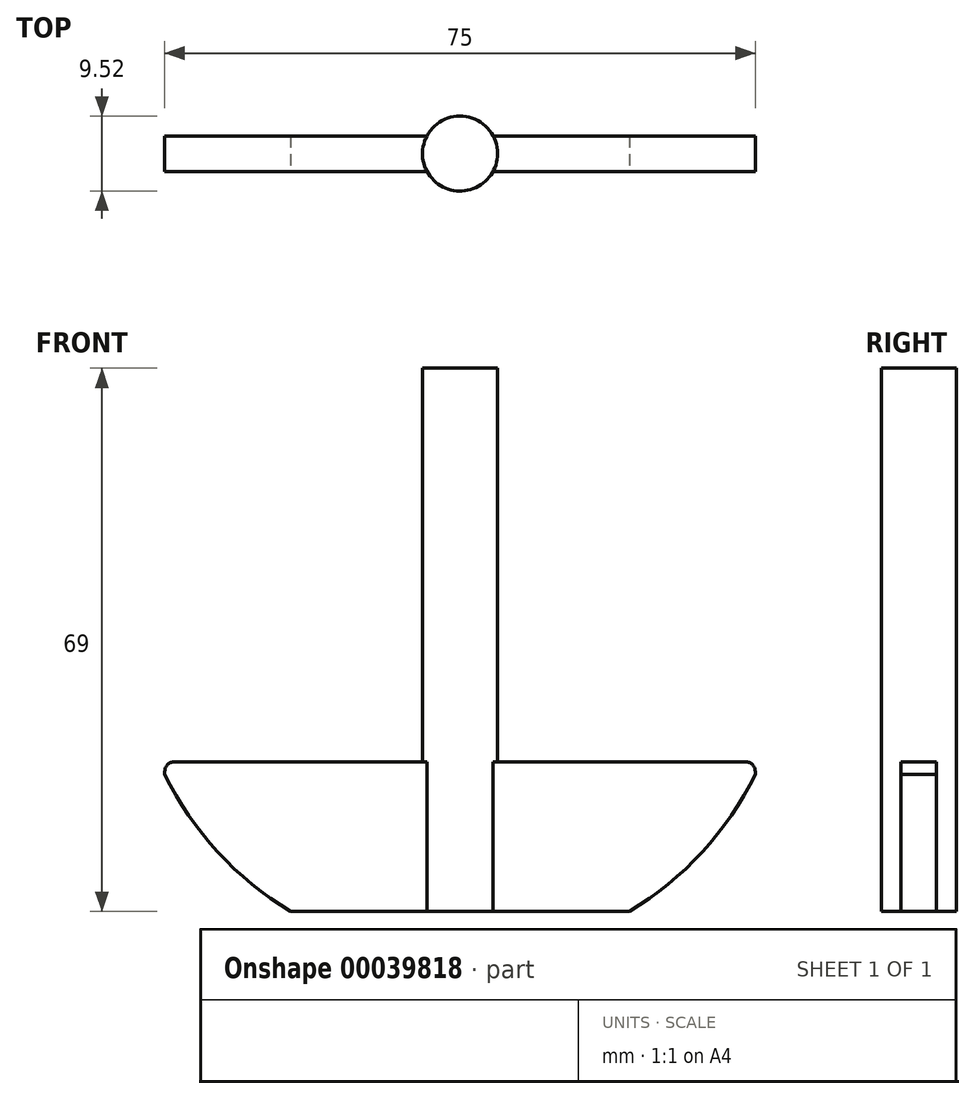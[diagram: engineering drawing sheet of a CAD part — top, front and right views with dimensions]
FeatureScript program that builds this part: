
annotation { "Feature Type Name" : "Feature", "Feature Type Description" : "" }
export const myFeature = defineFeature(function(context is Context, id is Id, definition is map)
    precondition{}
    {
        {
            var Q0;
            Q0=qCreatedBy(makeId("Top.planeOp"),FACE);
            var sketch = newSketch(context, id + "F0", { "sketchPlane" : qUnion([Q0])});
            skLineSegment(sketch, "E0.bottom", {"start": v(-7.96, 2) * mm, "end": v(25.34, 2) * mm});
            skLineSegment(sketch, "E0.top", {"start": v(-7.96, -2.5) * mm, "end": v(25.34, -2.5) * mm});
            skLineSegment(sketch, "E0.left", {"start": v(-7.96, 2) * mm, "end": v(-7.96, -2.5) * mm});
            skLineSegment(sketch, "E0.right", {"start": v(67.04, 2) * mm, "end": v(67.04, -2.5) * mm});
            skLineSegment(sketch, "E1", {"start": v(29.54, 2) * mm, "end": v(29.54, -16.68) * mm, "construction": true});
            skLineSegment(sketch, "E2", {"start": v(-7.96, -0.24) * mm, "end": v(37.53, -0.24) * mm, "construction": true});
            skArc(sketch, "E3", {"start": v(25.34, -2.5) * mm, "mid": v(29.54, -5) * mm, "end": v(33.73, -2.5) * mm});
            skArc(sketch, "E4.trimOffspring", {"start": v(33.73, 2) * mm, "mid": v(29.54, 4.52) * mm, "end": v(25.34, 2) * mm});
            skLineSegment(sketch, "E5.trimOffspring", {"start": v(33.73, 2) * mm, "end": v(67.04, 2) * mm});
            skLineSegment(sketch, "E6.trimOffspring", {"start": v(33.73, -2.5) * mm, "end": v(67.04, -2.5) * mm});
            skSolve(sketch);
        }
        {
            var Q0;
            Q0 = qSketchRegion(id + "F0", true);
            extrude(context, id + "F1", {"entities" : qUnion([Q0]), "depth" : 19 * mm});
        }
        {
            var Q0;
            Q0=makeQuery(id+"F1.opExtrude","CAP_FACE",FACE,{"disambiguationData":[OSD([sQuery(id+"F0.wireOp",EDGE,"E0.bottom"),sQuery(id+"F0.wireOp",EDGE,"E0.top"),sQuery(id+"F0.wireOp",EDGE,"E0.left"),sQuery(id+"F0.wireOp",EDGE,"E0.right"),sQuery(id+"F0.wireOp",EDGE,"E3"),sQuery(id+"F0.wireOp",EDGE,"E4.trimOffspring"),sQuery(id+"F0.wireOp",EDGE,"E5.trimOffspring"),sQuery(id+"F0.wireOp",EDGE,"E6.trimOffspring")])],"isStart":false});
            var sketch = newSketch(context, id + "F2", { "sketchPlane" : qUnion([Q0])});
            skCircle(sketch, "E7", {"center": v(29.54, -0.24) * mm, "radius": 4.76 * mm});
            skSolve(sketch);
        }
        {
            var Q0;
            Q0 = qSketchRegion(id + "F2", true);
            extrude(context, id + "F3", {"entities" : qUnion([Q0]), "operationType" : NewBodyOperationType.ADD, "depth" : 50 * mm});
        }
        {
            var Q0;
            Q0=makeQuery(id+"F1.opExtrude","SWEPT_FACE",FACE,{"disambiguationData":[OSD([sQuery(id+"F0.wireOp",EDGE,"E0.top")])]});
            var sketch = newSketch(context, id + "F4", { "sketchPlane" : qUnion([Q0])});
            skArc(sketch, "E8", {"start": v(-9.13, 19.99) * mm, "mid": v(-2.18, 8.6) * mm, "end": v(8, 0) * mm});
            skLineSegment(sketch, "E9", {"start": v(8, 0) * mm, "end": v(51.07, 0) * mm});
            skArc(sketch, "E10.trimOffspring", {"start": v(51.07, 0) * mm, "mid": v(61.3, 8.67) * mm, "end": v(68.27, 20.14) * mm});
            skLineSegment(sketch, "E11", {"start": v(8, 0) * mm, "end": v(-9.13, 0) * mm});
            skLineSegment(sketch, "E12", {"start": v(-9.13, 0) * mm, "end": v(-9.13, 19.99) * mm});
            skLineSegment(sketch, "E13", {"start": v(51.07, 0) * mm, "end": v(68.75, 0) * mm});
            skLineSegment(sketch, "E14", {"start": v(68.75, 0) * mm, "end": v(68.27, 20.14) * mm});
            skSolve(sketch);
        }
        {
            var Q0;
            Q0 = qSketchRegion(id + "F4", true);
            extrude(context, id + "F5", {"entities" : qUnion([Q0]), "operationType" : NewBodyOperationType.REMOVE, "endBound" : BoundingType.THROUGH_ALL, "oppositeDirection" : true, "depth" : 25 * mm});
        }
        {
            var Q0;
            Q0=makeQuery(id+"F1.opExtrude","CAP_EDGE",EDGE,{"disambiguationData":[OSD([sQuery(id+"F0.wireOp",EDGE,"E0.right")])],"isStart":false});
            var Q1;
            Q1=makeQuery(id+"F1.opExtrude","CAP_EDGE",EDGE,{"disambiguationData":[OSD([sQuery(id+"F0.wireOp",EDGE,"E0.left")])],"isStart":false});
            fillet(context, id + "F6", {"entities" : qUnion([Q0, Q1]), "radius" : 1.2 * mm, "tangentPropagation" : true, "allowEdgeOverflow" : false});
        }
    });
